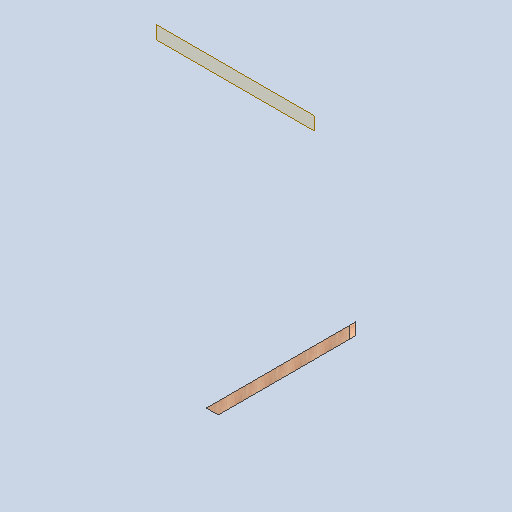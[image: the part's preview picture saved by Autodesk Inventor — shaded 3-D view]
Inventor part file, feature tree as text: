
AUTODESK INVENTOR PART (.ipt)
format: ipt  version: 2025 (Build 290162000, 162)  size: 146,432 bytes
history: native  units: in
note: dims shown in document units (in); Inventor stores cm internally (conversion verified against a paired STEP export)
features: other x4, reference x2, plane x1, extrude x1, sketch x1
ambient origin geometry x8: Origin, YZ Plane, XZ Plane, XY Plane, X Axis, Y Axis, Z Axis, Center Point
bodies: Solid1 (feature_tree)
feature tree (9):
  plane  "Work Plane1"
  extrude  "Extrusion1"  Depth=2.0in
  sketch  "Sketch1"  dims[d0=4.0in d1=4.0in d2=2.0in d3=0.0in]
  reference  "Reference1"
  reference  "Reference2"
  other  "<userpath>\Documents\GitHub\USCTigerBurn24\v2\Tiger.iam"
  other  "Tiger.iam"
  other  "2x4x48:14"
  other  "2x4x48:10"
